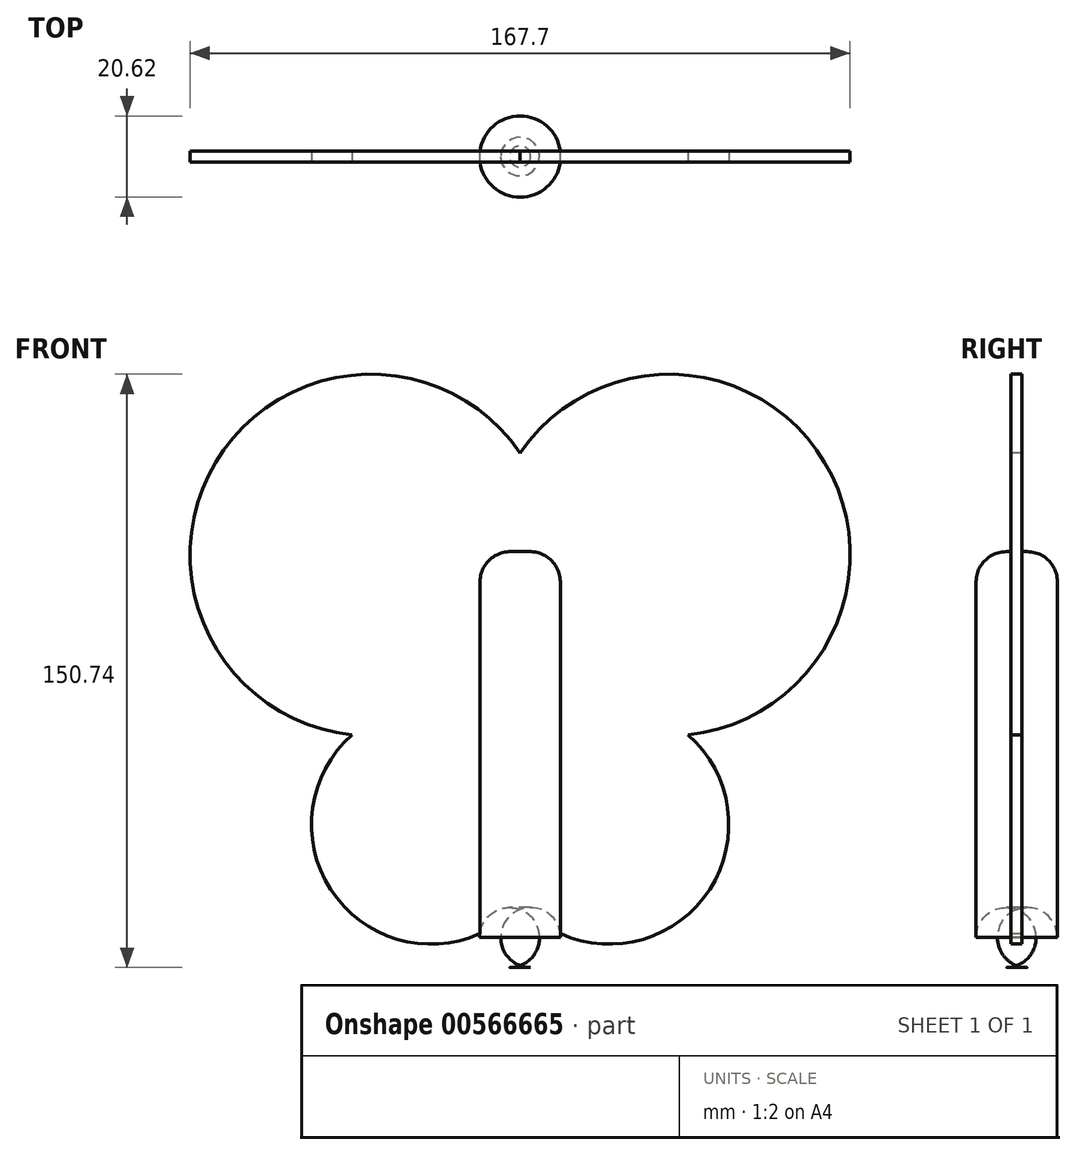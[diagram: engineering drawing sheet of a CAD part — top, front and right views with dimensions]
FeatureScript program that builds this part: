
annotation { "Feature Type Name" : "Feature", "Feature Type Description" : "" }
export const myFeature = defineFeature(function(context is Context, id is Id, definition is map)
    precondition{}
    {
        {
            var Q0;
            Q0=qCreatedBy(makeId("Front.planeOp"),FACE);
            var sketch = newSketch(context, id + "F0", { "sketchPlane" : qUnion([Q0])});
            skArc(sketch, "E0", {"start": v(-38.94, 6.32) * mm, "mid": v(-40.48, -37.88) * mm, "end": v(3.73, -36.74) * mm});
            skLineSegment(sketch, "E1", {"start": v(3.73, 31.5) * mm, "end": v(3.73, 15.48) * mm});
            skArc(sketch, "E2.MirrorCS", {"start": v(46.4, 6.32) * mm, "mid": v(47.94, -37.88) * mm, "end": v(3.73, -36.74) * mm});
            skArc(sketch, "E3.trimOffspring", {"start": v(3.73, 77.88) * mm, "mid": v(81.1, 75.5) * mm, "end": v(46.4, 6.32) * mm});
            skArc(sketch, "E4.trimOffspring", {"start": v(3.73, 77.88) * mm, "mid": v(-73.65, 75.5) * mm, "end": v(-38.94, 6.32) * mm});
            skPoint(sketch, "E5.MirrorCS.start.orphan", {"position": v(17.95, 12.66) * mm});
            skPoint(sketch, "E6.orphan", {"position": v(-10.5, 12.66) * mm});
            skSolve(sketch);
        }
        {
            var Q0;
            Q0=makeQuery(id+"F0.imprint","IMPRINT",FACE,{"disambiguationData":[TD([[makeQuery(id+"F0.imprint","IMPRINT",EDGE,{"derivedFrom":sQuery(id+"F0.wireOp",EDGE,"E0")}),1.0]])]});
            extrude(context, id + "F1", {"entities" : qUnion([Q0]), "oppositeDirection" : true, "depth" : 2.8 * mm, "offsetDistance" : 25.4 * mm});
        }
        {
            var Q0;
            Q0=qCreatedBy(makeId("Top.planeOp"),FACE);
            var sketch = newSketch(context, id + "F2", { "sketchPlane" : qUnion([Q0])});
            skCircle(sketch, "E7", {"center": v(3.73, 1.46) * mm, "radius": 10.31 * mm});
            skSolve(sketch);
        }
        {
            var Q0;
            Q0=makeQuery(id+"F2.imprint","IMPRINT",FACE,{"disambiguationData":[TD([[makeQuery(id+"F2.imprint","IMPRINT",EDGE,{"derivedFrom":sQuery(id+"F2.wireOp",EDGE,"E7")}),1.0]])]});
            extrude(context, id + "F3", {"entities" : qUnion([Q0]), "operationType" : NewBodyOperationType.ADD, "endBound" : BoundingType.SYMMETRIC, "depth" : 105.66 * mm, "offsetDistance" : 25.4 * mm});
        }
        {
            var Q0;
            {var subQ0=sQuery(id+"F2.wireOp",EDGE,"E7");Q0=makeQuery(id+"F3.boolean.opBoolean","SPLIT",EDGE,{"disambiguationData":[TD([makeQuery(id+"F1.opExtrude","CAP_FACE",FACE,{"disambiguationData":[OSD([sQuery(id+"F0.wireOp",EDGE,"E0"),sQuery(id+"F0.wireOp",EDGE,"E2.MirrorCS"),sQuery(id+"F0.wireOp",EDGE,"E3.trimOffspring"),sQuery(id+"F0.wireOp",EDGE,"E4.trimOffspring")])],"isStart":true})])],"derivedFrom":makeQuery(id+"F3.opExtrude","CAP_EDGE",EDGE,{"disambiguationData":[OSD([subQ0])],"isStart":false})});}
            var Q1;
            Q1=makeQuery(id+"F3.opExtrude","CAP_FACE",FACE,{"disambiguationData":[OSD([sQuery(id+"F2.wireOp",EDGE,"E7")])],"isStart":true});
            var Q2;
            {var subQ0=sQuery(id+"F2.wireOp",EDGE,"E7");Q2=makeQuery(id+"F3.boolean.opBoolean","SPLIT",EDGE,{"disambiguationData":[TD([makeQuery(id+"F1.opExtrude","CAP_FACE",FACE,{"disambiguationData":[OSD([sQuery(id+"F0.wireOp",EDGE,"E0"),sQuery(id+"F0.wireOp",EDGE,"E2.MirrorCS"),sQuery(id+"F0.wireOp",EDGE,"E3.trimOffspring"),sQuery(id+"F0.wireOp",EDGE,"E4.trimOffspring")])],"isStart":false})])],"derivedFrom":makeQuery(id+"F3.opExtrude","CAP_EDGE",EDGE,{"disambiguationData":[OSD([subQ0])],"isStart":false})});}
            fillet(context, id + "F4", {"entities" : qUnion([Q0, Q1, Q2]), "radius" : 7.62 * mm, "tangentPropagation" : true, "allowEdgeOverflow" : false});
        }
    });
